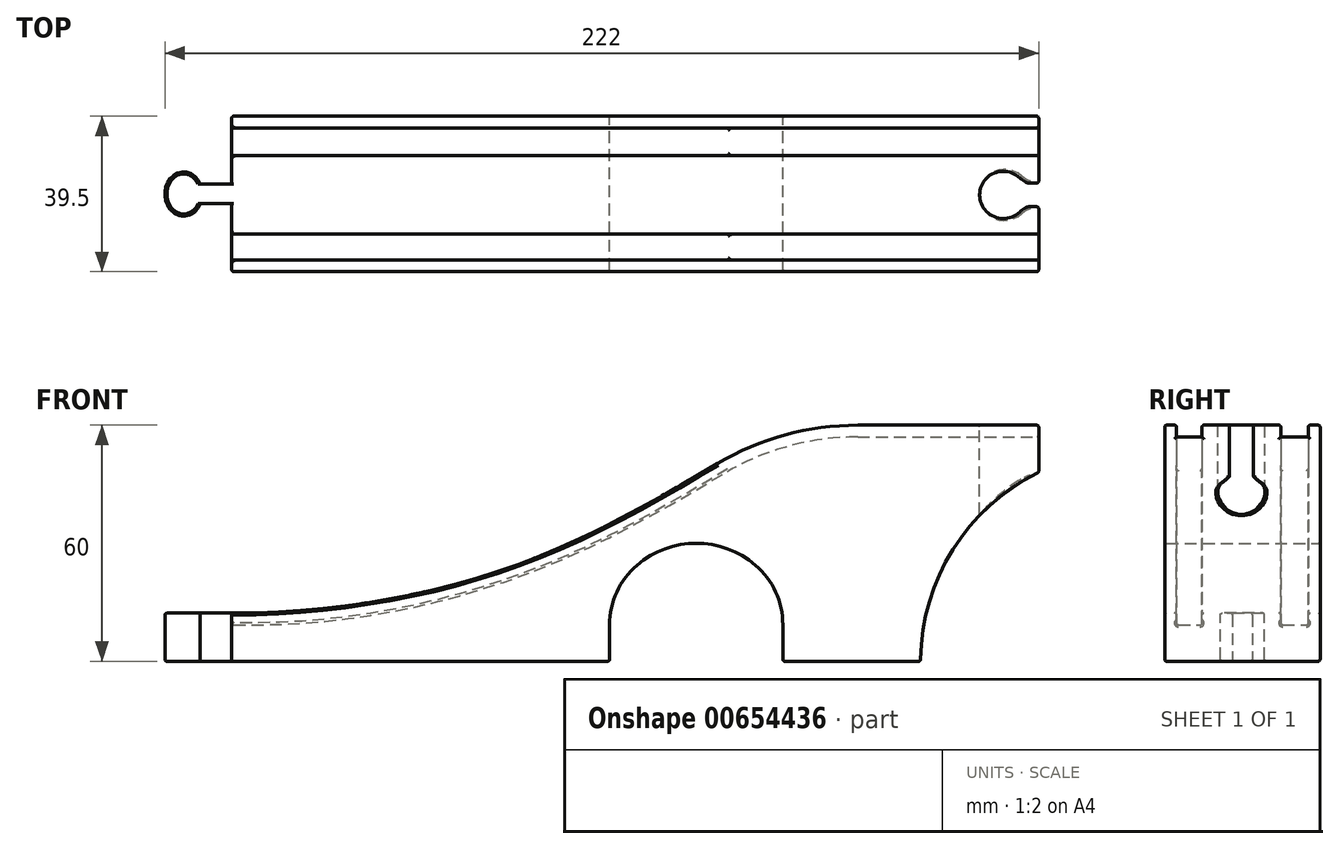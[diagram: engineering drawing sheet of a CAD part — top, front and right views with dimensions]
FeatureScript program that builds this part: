
annotation { "Feature Type Name" : "Feature", "Feature Type Description" : "" }
export const myFeature = defineFeature(function(context is Context, id is Id, definition is map)
    precondition{}
    {
        {
            var Q0;
            Q0=qCreatedBy(makeId("Front.planeOp"),FACE);
            var sketch = newSketch(context, id + "F0", { "sketchPlane" : qUnion([Q0])});
            skLineSegment(sketch, "E0.bottom", {"start": v(0, 0) * mm, "end": v(-96, 0) * mm});
            skLineSegment(sketch, "E0.left", {"start": v(0, 0) * mm, "end": v(0, 12) * mm});
            skLineSegment(sketch, "E0.right", {"start": v(-96, 0) * mm, "end": v(-96, 12.25) * mm});
            skArc(sketch, "E1", {"start": v(37.04, 24.42) * mm, "mid": v(22, 30) * mm, "end": v(6.96, 24.42) * mm});
            skLineSegment(sketch, "E2", {"start": v(0, 0) * mm, "end": v(44, 0) * mm, "construction": true});
            skLineSegment(sketch, "E3", {"start": v(22, 0) * mm, "end": v(22, 30) * mm, "construction": true});
            skLineSegment(sketch, "E4", {"start": v(0, 9.26) * mm, "end": v(0, 12) * mm});
            skLineSegment(sketch, "E5", {"start": v(44, 0) * mm, "end": v(44, 27.9) * mm});
            skLineSegment(sketch, "E6.bottom", {"start": v(44, 0) * mm, "end": v(79, 0) * mm});
            skLineSegment(sketch, "E6.top", {"start": v(63.07, 60) * mm, "end": v(79, 60) * mm});
            skLineSegment(sketch, "E6.left", {"start": v(44, 0) * mm, "end": v(44, 9.26) * mm});
            skArc(sketch, "E7", {"start": v(109, 48) * mm, "mid": v(87.12, 28.3) * mm, "end": v(79, 0) * mm});
            skLineSegment(sketch, "E8", {"start": v(117, 60) * mm, "end": v(117, 48) * mm, "construction": true});
            skLineSegment(sketch, "E9", {"start": v(117, 48) * mm, "end": v(109, 48) * mm, "construction": true});
            skLineSegment(sketch, "E10.top", {"start": v(109, 60) * mm, "end": v(79, 60) * mm});
            skLineSegment(sketch, "E10.left", {"start": v(109, 48) * mm, "end": v(109, 60) * mm});
            skFitSpline(sketch, "E11", {"points": [v(43.96, 60) * mm, v(-19.75, 25.96) * mm, v(-96, 12.25) * mm], "startDerivative": vector(-126.55, -73.25) * mm, "endDerivative": vector(-154.32, 0) * mm});
            skArc(sketch, "E12.filletArc", {"start": v(63.07, 60) * mm, "mid": v(44.57, 57.51) * mm, "end": v(27.4, 50.23) * mm});
            skPoint(sketch, "E13.visualSharp", {"position": v(0, 13.87) * mm});
            skArc(sketch, "E13.filletArc", {"start": v(6.96, 24.42) * mm, "mid": v(1.82, 17.6) * mm, "end": v(0, 9.26) * mm});
            skArc(sketch, "E14.filletArc", {"start": v(44, 9.26) * mm, "mid": v(42.18, 17.6) * mm, "end": v(37.04, 24.42) * mm});
            skPoint(sketch, "E15.end.orphan", {"position": v(79, 48) * mm});
            skFitSpline(sketch, "E16.0", {"points": [v(45.47, 57.4) * mm, v(40.22, 54.37) * mm, v(29.76, 48.12) * mm, v(16.53, 40.33) * mm, v(5.69, 34.4) * mm, v(-2.6, 30.16) * mm, v(-9.7, 26.87) * mm, v(-15.49, 24.42) * mm, v(-21.37, 22.1) * mm, v(-28.88, 19.46) * mm, v(-41.18, 15.8) * mm, v(-57, 12.31) * mm, v(-76.42, 9.8) * mm, v(-89.48, 9.25) * mm, v(-96, 9.25) * mm]});
            skArc(sketch, "E16.1", {"start": v(63.07, 57) * mm, "mid": v(45.37, 54.62) * mm, "end": v(28.92, 47.65) * mm});
            skLineSegment(sketch, "E16.2", {"start": v(63.07, 57) * mm, "end": v(79, 57) * mm});
            skLineSegment(sketch, "E16.3", {"start": v(109, 57) * mm, "end": v(79, 57) * mm});
            skSolve(sketch);
        }
        {
            var Q0;
            {var subQ3=sQuery(id+"F0.wireOp",EDGE,"E0.bottom");Q0=makeQuery(id+"F0.imprint","IMPRINT",FACE,{"disambiguationData":[TD([[makeQuery(id+"F0.imprint","IMPRINT",EDGE,{"derivedFrom":subQ3}),-1.0]])]});}
            extrude(context, id + "F1", {"entities" : qUnion([Q0]), "depth" : 39.5 * mm, "offsetDistance" : 25 * mm});
        }
        {
            var Q0;
            Q0=makeQuery(id+"F0.imprint","IMPRINT",FACE,{"disambiguationData":[TD([[makeQuery(id+"F0.imprint","IMPRINT",EDGE,{"derivedFrom":sQuery(id+"F0.wireOp",EDGE,"E6.top")}),-1.0]])]});
            extrude(context, id + "F2", {"entities" : qUnion([Q0]), "operationType" : NewBodyOperationType.ADD, "depth" : 39.5 * mm, "offsetDistance" : 25 * mm});
        }
        {
            var Q0;
            Q0=makeQuery(id+"F0.imprint","IMPRINT",FACE,{"disambiguationData":[TD([[makeQuery(id+"F0.imprint","IMPRINT",EDGE,{"derivedFrom":sQuery(id+"F0.wireOp",EDGE,"E6.top")}),-1.0]])]});
            extrude(context, id + "F3", {"entities" : qUnion([Q0]), "operationType" : NewBodyOperationType.REMOVE, "depth" : 36.5 * mm, "offsetDistance" : 25 * mm});
        }
        {
            var Q0;
            Q0=makeQuery(id+"F0.imprint","IMPRINT",FACE,{"disambiguationData":[TD([[makeQuery(id+"F0.imprint","IMPRINT",EDGE,{"derivedFrom":sQuery(id+"F0.wireOp",EDGE,"E6.top")}),-1.0]])]});
            extrude(context, id + "F4", {"entities" : qUnion([Q0]), "operationType" : NewBodyOperationType.ADD, "depth" : 30 * mm, "offsetDistance" : 25 * mm});
        }
        {
            var Q0;
            Q0=makeQuery(id+"F0.imprint","IMPRINT",FACE,{"disambiguationData":[TD([[makeQuery(id+"F0.imprint","IMPRINT",EDGE,{"derivedFrom":sQuery(id+"F0.wireOp",EDGE,"E6.top")}),-1.0]])]});
            extrude(context, id + "F5", {"entities" : qUnion([Q0]), "operationType" : NewBodyOperationType.REMOVE, "depth" : 10 * mm, "offsetDistance" : 25 * mm});
        }
        {
            var Q0;
            Q0=makeQuery(id+"F0.imprint","IMPRINT",FACE,{"disambiguationData":[TD([[makeQuery(id+"F0.imprint","IMPRINT",EDGE,{"derivedFrom":sQuery(id+"F0.wireOp",EDGE,"E6.top")}),-1.0]])]});
            extrude(context, id + "F6", {"entities" : qUnion([Q0]), "operationType" : NewBodyOperationType.ADD, "depth" : 3 * mm, "offsetDistance" : 25 * mm});
        }
        {
            var Q0;
            Q0=makeQuery(id+"F4.opExtrude","SWEPT_FACE",FACE,{"disambiguationData":[OSD([sQuery(id+"F0.wireOp",EDGE,"E6.top"),sQuery(id+"F0.wireOp",EDGE,"E10.top")])]});
            var sketch = newSketch(context, id + "F7", { "sketchPlane" : qUnion([Q0])});
            skLineSegment(sketch, "E17.bottom", {"start": v(106.63, -23) * mm, "end": v(109, -23) * mm});
            skLineSegment(sketch, "E17.top", {"start": v(106.63, -17) * mm, "end": v(109, -17) * mm});
            skPoint(sketch, "E17.middle", {"position": v(109, -20) * mm});
            skArc(sketch, "E18", {"start": v(104.18, -15.7) * mm, "mid": v(94, -20) * mm, "end": v(104.18, -24.3) * mm});
            skPoint(sketch, "E18.centerSnap0", {"position": v(106, -20) * mm});
            skLineSegment(sketch, "E19", {"start": v(105.48, -16.64) * mm, "end": v(104.42, -15.9) * mm});
            skLineSegment(sketch, "E20", {"start": v(105.48, -23.36) * mm, "end": v(104.42, -24.1) * mm});
            skPoint(sketch, "E21.visualSharp", {"position": v(106, -17) * mm});
            skArc(sketch, "E21.filletArc", {"start": v(105.48, -16.64) * mm, "mid": v(106.03, -16.9) * mm, "end": v(106.63, -17) * mm});
            skPoint(sketch, "E22.visualSharp", {"position": v(106, -23) * mm});
            skArc(sketch, "E22.filletArc", {"start": v(106.63, -23) * mm, "mid": v(106.03, -23.1) * mm, "end": v(105.48, -23.36) * mm});
            skPoint(sketch, "E23.visualSharp", {"position": v(104.28, -15.8) * mm});
            skArc(sketch, "E23.filletArc", {"start": v(104.18, -15.7) * mm, "mid": v(104.3, -15.8) * mm, "end": v(104.42, -15.9) * mm});
            skPoint(sketch, "E24.visualSharp", {"position": v(104.28, -24.2) * mm});
            skArc(sketch, "E24.filletArc", {"start": v(104.42, -24.1) * mm, "mid": v(104.3, -24.2) * mm, "end": v(104.18, -24.3) * mm});
            skLineSegment(sketch, "E25", {"start": v(109, -20) * mm, "end": v(109, -17) * mm});
            skLineSegment(sketch, "E26", {"start": v(109, -20) * mm, "end": v(109, -23) * mm});
            skLineSegment(sketch, "E27", {"start": v(109, -23) * mm, "end": v(109, -20) * mm});
            skSolve(sketch);
        }
        {
            var Q0;
            Q0=makeQuery(id+"F7.imprint","IMPRINT",FACE,{"disambiguationData":[TD([[makeQuery(id+"F7.imprint","IMPRINT",EDGE,{"derivedFrom":sQuery(id+"F7.wireOp",EDGE,"E17.bottom")}),1.0]])]});
            extrude(context, id + "F8", {"entities" : qUnion([Q0]), "operationType" : NewBodyOperationType.REMOVE, "oppositeDirection" : true, "depth" : 25 * mm, "offsetDistance" : 25 * mm});
        }
        {
            var Q0;
            Q0=makeQuery(id+"F1.opExtrude","SWEPT_FACE",FACE,{"disambiguationData":[OSD([sQuery(id+"F0.wireOp",EDGE,"E0.bottom")])]});
            var sketch = newSketch(context, id + "F9", { "sketchPlane" : qUnion([Q0])});
            skPoint(sketch, "E28.middle", {"position": v(-96, 19.75) * mm});
            skEllipticalArc(sketch, "E29", {});
            skPoint(sketch, "E29.centerSnap0", {"position": v(-113, 19.75) * mm});
            skPoint(sketch, "E30.orphan", {"position": v(-113, 25.35) * mm});
            skPoint(sketch, "E31.orphan", {"position": v(-113, 14.15) * mm});
            skLineSegment(sketch, "E32.bottom", {"start": v(-104, 22.25) * mm, "end": v(-96, 22.25) * mm});
            skLineSegment(sketch, "E32.top", {"start": v(-104, 17.25) * mm, "end": v(-96, 17.25) * mm});
            skPoint(sketch, "E32.left.start.orphan", {"position": v(-106, 22.25) * mm});
            skPoint(sketch, "E33.orphan", {"position": v(-106, 17.25) * mm});
            skLineSegment(sketch, "E34", {"start": v(-96, 25.35) * mm, "end": v(-96, 14.15) * mm});
            skPoint(sketch, "E32.right.start.orphan", {"position": v(-86, 22.25) * mm});
            skPoint(sketch, "E35.orphan", {"position": v(-86, 17.25) * mm});
            skPoint(sketch, "E28.right.start.orphan", {"position": v(-79, 25.35) * mm});
            skPoint(sketch, "E36.orphan", {"position": v(-79, 14.15) * mm});
            const initialGuessF9  = {"E29": [-0.10825, 0.01975, 0, 1, 0.0056, 0.00475, 5.175159098176783, 4.249618862592596]};
            skSetInitialGuess(sketch, initialGuessF9);
            skSolve(sketch);
        }
        {
            var Q0;
            Q0=makeQuery(id+"F9.imprint","IMPRINT",FACE,{"disambiguationData":[TD([[makeQuery(id+"F9.imprint","IMPRINT",EDGE,{"derivedFrom":sQuery(id+"F9.wireOp",EDGE,"E29")}),1.0]])]});
            extrude(context, id + "F10", {"entities" : qUnion([Q0]), "operationType" : NewBodyOperationType.ADD, "oppositeDirection" : true, "depth" : 12.25 * mm, "offsetDistance" : 25 * mm});
        }
        {
            var Q0;
            Q0=makeQuery(id+"F2.opExtrude","SWEPT_FACE",FACE,{"disambiguationData":[OSD([sQuery(id+"F0.wireOp",EDGE,"E11")])]});
            var Q1;
            Q1=makeQuery(id+"F6.opExtrude","SWEPT_FACE",FACE,{"disambiguationData":[OSD([sQuery(id+"F0.wireOp",EDGE,"E11")])]});
            var Q2;
            {var subQ0=sQuery(id+"F0.wireOp",EDGE,"E11");var subQ1=sQuery(id+"F0.wireOp",EDGE,"E0.right");var subQ2=sQuery(id+"F9.wireOp",EDGE,"E32.bottom");Q2=makeQuery(id+"F10.boolean.opBoolean","SPLIT",EDGE,{"disambiguationData":[TD([makeQuery(id+"F10.opExtrude","SWEPT_FACE",FACE,{"disambiguationData":[OSD([subQ2])]})])],"derivedFrom":makeQuery(id+"F4.opExtrude","SWEPT_EDGE",EDGE,{"disambiguationData":[OSD([subQ1,subQ0])]})});}
            var Q3;
            Q3=makeQuery(id+"F10.opExtrude","CAP_EDGE",EDGE,{"disambiguationData":[OSD([sQuery(id+"F9.wireOp",EDGE,"E29")])],"isStart":false});
            var Q4;
            Q4=makeQuery(id+"F10.opExtrude","CAP_EDGE",EDGE,{"disambiguationData":[OSD([sQuery(id+"F9.wireOp",EDGE,"E29")])],"isStart":true});
            var Q5;
            Q5=makeQuery(id+"F4.opExtrude","SWEPT_FACE",FACE,{"disambiguationData":[OSD([sQuery(id+"F0.wireOp",EDGE,"E11")])]});
            var Q6;
            Q6=makeQuery(id+"F3.boolean.opBoolean","COPY",FACE,{"derivedFrom":makeQuery(id+"F3.opExtrude","SWEPT_FACE",FACE,{"disambiguationData":[OSD([sQuery(id+"F0.wireOp",EDGE,"E16.0")])]})});
            var Q7;
            Q7=makeQuery(id+"F5.boolean.opBoolean","COPY",FACE,{"derivedFrom":makeQuery(id+"F5.opExtrude","SWEPT_FACE",FACE,{"disambiguationData":[OSD([sQuery(id+"F0.wireOp",EDGE,"E16.0")])]})});
            var Q8;
            {var subQ0=sQuery(id+"F0.wireOp",EDGE,"E16.3");var subQ1=sQuery(id+"F0.wireOp",EDGE,"E16.2");var subQ2=sQuery(id+"F0.wireOp",EDGE,"E16.1");var subQ3=sQuery(id+"F0.wireOp",EDGE,"E16.0");var subQ4=sQuery(id+"F0.wireOp",EDGE,"E10.left");var subQ5=sQuery(id+"F0.wireOp",EDGE,"E0.right");Q8=makeQuery(id+"F2.boolean.opBoolean","MERGE",FACE,{"derivedFrom":[makeQuery(id+"F1.opExtrude","CAP_FACE",FACE,{"disambiguationData":[OSD([sQuery(id+"F0.wireOp",EDGE,"E0.bottom"),sQuery(id+"F0.wireOp",EDGE,"E0.left"),subQ5,sQuery(id+"F0.wireOp",EDGE,"E1"),sQuery(id+"F0.wireOp",EDGE,"E4"),sQuery(id+"F0.wireOp",EDGE,"E6.bottom"),sQuery(id+"F0.wireOp",EDGE,"E6.left"),sQuery(id+"F0.wireOp",EDGE,"E7"),subQ4,sQuery(id+"F0.wireOp",EDGE,"E13.filletArc"),sQuery(id+"F0.wireOp",EDGE,"E14.filletArc"),subQ3,subQ2,subQ1,subQ0])],"isStart":false}),makeQuery(id+"F2.opExtrude","CAP_FACE",FACE,{"disambiguationData":[OSD([subQ5,sQuery(id+"F0.wireOp",EDGE,"E6.top"),sQuery(id+"F0.wireOp",EDGE,"E10.top"),subQ4,sQuery(id+"F0.wireOp",EDGE,"E11"),sQuery(id+"F0.wireOp",EDGE,"E12.filletArc"),subQ3,subQ2,subQ1,subQ0])],"isStart":false})]});}
            var Q9;
            {var subQ0=sQuery(id+"F0.wireOp",EDGE,"E0.right");var subQ6=sQuery(id+"F0.wireOp",EDGE,"E0.bottom");var subQ7=sQuery(id+"F9.wireOp",EDGE,"E32.bottom");Q9=makeQuery(id+"F10.boolean.opBoolean","SPLIT",EDGE,{"disambiguationData":[TD([makeQuery(id+"F10.opExtrude","SWEPT_FACE",FACE,{"disambiguationData":[OSD([subQ7])]})])],"derivedFrom":makeQuery(id+"F1.opExtrude","SWEPT_EDGE",EDGE,{"disambiguationData":[OSD([subQ6,subQ0])]})});}
            var Q10;
            {var subQ0=sQuery(id+"F0.wireOp",EDGE,"E16.3");var subQ1=sQuery(id+"F0.wireOp",EDGE,"E16.2");var subQ2=sQuery(id+"F0.wireOp",EDGE,"E16.1");var subQ3=sQuery(id+"F0.wireOp",EDGE,"E16.0");var subQ4=sQuery(id+"F0.wireOp",EDGE,"E12.filletArc");var subQ5=sQuery(id+"F0.wireOp",EDGE,"E11");var subQ6=sQuery(id+"F0.wireOp",EDGE,"E10.left");var subQ7=sQuery(id+"F0.wireOp",EDGE,"E10.top");var subQ8=sQuery(id+"F0.wireOp",EDGE,"E6.top");var subQ9=sQuery(id+"F0.wireOp",EDGE,"E0.right");Q10=makeQuery(id+"F6.boolean.opBoolean","MERGE",FACE,{"derivedFrom":[makeQuery(id+"F4.boolean.opBoolean","MERGE",FACE,{"derivedFrom":[makeQuery(id+"F2.boolean.opBoolean","MERGE",FACE,{"derivedFrom":[makeQuery(id+"F1.opExtrude","CAP_FACE",FACE,{"disambiguationData":[OSD([sQuery(id+"F0.wireOp",EDGE,"E0.bottom"),sQuery(id+"F0.wireOp",EDGE,"E0.left"),subQ9,sQuery(id+"F0.wireOp",EDGE,"E1"),sQuery(id+"F0.wireOp",EDGE,"E4"),sQuery(id+"F0.wireOp",EDGE,"E6.bottom"),sQuery(id+"F0.wireOp",EDGE,"E6.left"),sQuery(id+"F0.wireOp",EDGE,"E7"),subQ6,sQuery(id+"F0.wireOp",EDGE,"E13.filletArc"),sQuery(id+"F0.wireOp",EDGE,"E14.filletArc"),subQ3,subQ2,subQ1,subQ0])],"isStart":true}),makeQuery(id+"F2.opExtrude","CAP_FACE",FACE,{"disambiguationData":[OSD([subQ9,subQ8,subQ7,subQ6,subQ5,subQ4,subQ3,subQ2,subQ1,subQ0])],"isStart":true})]}),makeQuery(id+"F4.opExtrude","CAP_FACE",FACE,{"disambiguationData":[OSD([subQ9,subQ8,subQ7,subQ6,subQ5,subQ4,subQ3,subQ2,subQ1,subQ0])],"isStart":true})]}),makeQuery(id+"F6.opExtrude","CAP_FACE",FACE,{"disambiguationData":[OSD([subQ9,subQ8,subQ7,subQ6,subQ5,subQ4,subQ3,subQ2,subQ1,subQ0])],"isStart":true})]});}
            var Q11;
            {var subQ0=sQuery(id+"F9.wireOp",EDGE,"E32.top");var subQ1=sQuery(id+"F0.wireOp",EDGE,"E0.right");var subQ11=sQuery(id+"F0.wireOp",EDGE,"E0.bottom");Q11=makeQuery(id+"F10.boolean.opBoolean","SPLIT",EDGE,{"disambiguationData":[TD([makeQuery(id+"F10.opExtrude","SWEPT_FACE",FACE,{"disambiguationData":[OSD([subQ0])]})])],"derivedFrom":makeQuery(id+"F1.opExtrude","SWEPT_EDGE",EDGE,{"disambiguationData":[OSD([subQ11,subQ1])]})});}
            var Q12;
            {var subQ8=sQuery(id+"F0.wireOp",EDGE,"E10.left");Q12=makeQuery(id+"F8.boolean.opBoolean","SPLIT",FACE,{"disambiguationData":[TD([makeQuery(id+"F8.opExtrude","SWEPT_FACE",FACE,{"disambiguationData":[OSD([sQuery(id+"F7.wireOp",EDGE,"E17.top")])]})])],"derivedFrom":makeQuery(id+"F6.boolean.opBoolean","MERGE",FACE,{"derivedFrom":[makeQuery(id+"F4.boolean.opBoolean","MERGE",FACE,{"derivedFrom":[makeQuery(id+"F2.boolean.opBoolean","MERGE",FACE,{"derivedFrom":[makeQuery(id+"F1.opExtrude","SWEPT_FACE",FACE,{"disambiguationData":[OSD([subQ8])]}),makeQuery(id+"F2.opExtrude","SWEPT_FACE",FACE,{"disambiguationData":[OSD([subQ8])]})]}),makeQuery(id+"F4.opExtrude","SWEPT_FACE",FACE,{"disambiguationData":[OSD([subQ8])]})]}),makeQuery(id+"F6.opExtrude","SWEPT_FACE",FACE,{"disambiguationData":[OSD([subQ8])]})]})});}
            var Q13;
            {var subQ8=sQuery(id+"F0.wireOp",EDGE,"E10.left");Q13=makeQuery(id+"F8.boolean.opBoolean","SPLIT",FACE,{"disambiguationData":[TD([makeQuery(id+"F8.opExtrude","SWEPT_FACE",FACE,{"disambiguationData":[OSD([sQuery(id+"F7.wireOp",EDGE,"E17.bottom")])]})])],"derivedFrom":makeQuery(id+"F6.boolean.opBoolean","MERGE",FACE,{"derivedFrom":[makeQuery(id+"F4.boolean.opBoolean","MERGE",FACE,{"derivedFrom":[makeQuery(id+"F2.boolean.opBoolean","MERGE",FACE,{"derivedFrom":[makeQuery(id+"F1.opExtrude","SWEPT_FACE",FACE,{"disambiguationData":[OSD([subQ8])]}),makeQuery(id+"F2.opExtrude","SWEPT_FACE",FACE,{"disambiguationData":[OSD([subQ8])]})]}),makeQuery(id+"F4.opExtrude","SWEPT_FACE",FACE,{"disambiguationData":[OSD([subQ8])]})]}),makeQuery(id+"F6.opExtrude","SWEPT_FACE",FACE,{"disambiguationData":[OSD([subQ8])]})]})});}
            var Q14;
            Q14=makeQuery(id+"F8.boolean.opBoolean","COPY",FACE,{"derivedFrom":makeQuery(id+"F8.opExtrude","SWEPT_FACE",FACE,{"disambiguationData":[OSD([sQuery(id+"F7.wireOp",EDGE,"E18")])]})});
            var Q15;
            Q15=makeQuery(id+"F1.opExtrude","SWEPT_FACE",FACE,{"disambiguationData":[OSD([sQuery(id+"F0.wireOp",EDGE,"E6.bottom")])]});
            var Q16;
            Q16=makeQuery(id+"F1.opExtrude","SWEPT_EDGE",EDGE,{"disambiguationData":[OSD([sQuery(id+"F0.wireOp",EDGE,"E0.bottom"),sQuery(id+"F0.wireOp",EDGE,"E0.left")])]});
            fillet(context, id + "F11", {"entities" : qUnion([Q0, Q1, Q2, Q3, Q4, Q5, Q6, Q7, Q8, Q9, Q10, Q11, Q12, Q13, Q14, Q15, Q16]), "radius" : 0.5 * mm, "tangentPropagation" : true, "allowEdgeOverflow" : false});
        }
    });
